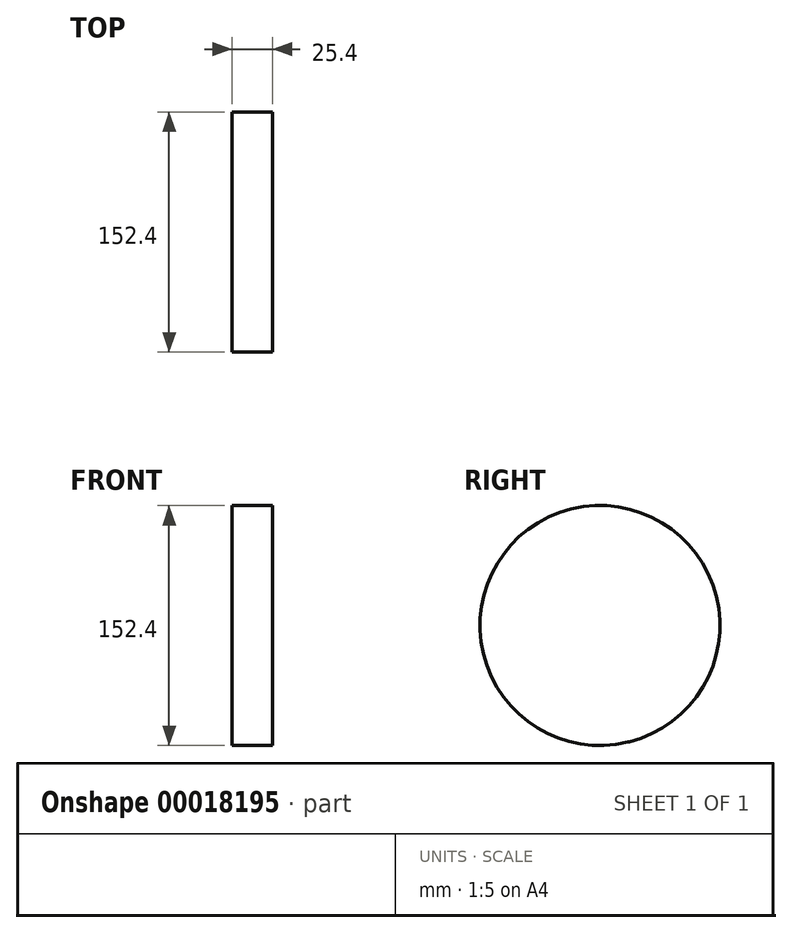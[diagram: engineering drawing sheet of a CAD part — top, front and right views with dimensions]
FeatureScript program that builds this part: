
annotation { "Feature Type Name" : "Feature", "Feature Type Description" : "" }
export const myFeature = defineFeature(function(context is Context, id is Id, definition is map)
    precondition{}
    {
        {
            var Q0;
            Q0=qCreatedBy(makeId("Right.planeOp"),FACE);
            var sketch = newSketch(context, id + "F0", { "sketchPlane" : qUnion([Q0])});
            skCircle(sketch, "E0", {"center": v(0, 0) * mm, "radius": 76.2 * mm});
            skCircle(sketch, "E1", {"center": v(215.15, 0) * mm, "radius": 25.4 * mm});
            skLineSegment(sketch, "E2", {"start": v(17.86, 74.08) * mm, "end": v(215.15, 25.4) * mm});
            skLineSegment(sketch, "E3", {"start": v(17.86, -74.08) * mm, "end": v(215.15, -25.4) * mm});
            skSolve(sketch);
        }
        {
            var Q0;
            {var subQ0=sQuery(id+"F0.wireOp",EDGE,"E2");var subQ1=sQuery(id+"F0.wireOp",EDGE,"E0");var subQ3=makeQuery(id+"F0.imprint","INTERSECT",VERTEX,{"disambiguationData":[OD(0.0)],"derivedFrom":[subQ1,subQ0]});Q0=makeQuery(id+"F0.imprint","IMPRINT",FACE,{"disambiguationData":[TD([[makeQuery(id+"F0.imprint","IMPRINT",EDGE,{"disambiguationData":[TD([[subQ3,1.0]])],"derivedFrom":subQ1}),1.0]])]});}
            var Q1;
            {var subQ1=sQuery(id+"F0.wireOp",EDGE,"E0");var subQ4=sQuery(id+"F0.wireOp",EDGE,"E2");var subQ6=makeQuery(id+"F0.imprint","INTERSECT",VERTEX,{"disambiguationData":[OD(0.0)],"derivedFrom":[subQ1,subQ4]});Q1=makeQuery(id+"F0.imprint","IMPRINT",FACE,{"disambiguationData":[TD([[makeQuery(id+"F0.imprint","IMPRINT",EDGE,{"disambiguationData":[TD([[subQ6,-1.0]])],"derivedFrom":subQ1}),1.0]])]});}
            extrude(context, id + "F1", {"entities" : qUnion([Q0, Q1]), "depth" : 25.4 * mm});
        }
    });
